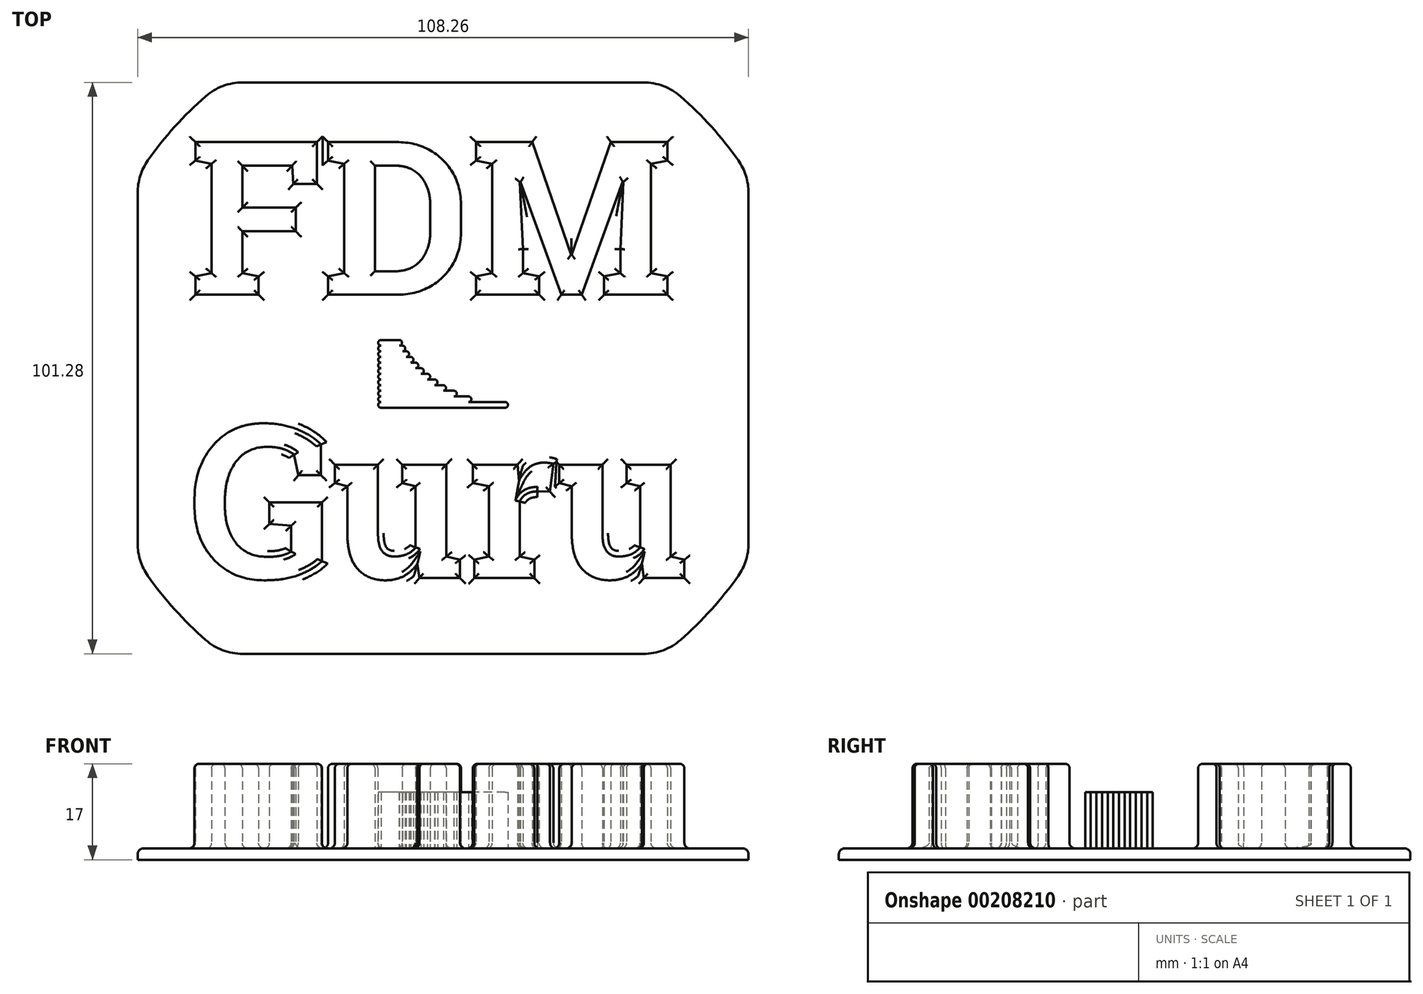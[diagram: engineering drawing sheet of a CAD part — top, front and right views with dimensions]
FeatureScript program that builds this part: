
annotation { "Feature Type Name" : "Feature", "Feature Type Description" : "" }
export const myFeature = defineFeature(function(context is Context, id is Id, definition is map)
    precondition{}
    {
        {
            var Q0;
            Q0=qCreatedBy(makeId("Top.planeOp"),FACE);
            var sketch = newSketch(context, id + "F0", { "sketchPlane" : qUnion([Q0])});
            skText(sketch, "E0", { "text": "FDM\nGuru", "fontName": "RobotoSlab-Bold.ttf"});
            const initialGuessF0  = {"E0": [-0.04493, 0.0016, 1, 0, 0.0274]};
            skSetInitialGuess(sketch, initialGuessF0);
            skSolve(sketch);
        }
        {
            var Q0;
            Q0 = qSketchRegion(id + "F0", true);
            extrude(context, id + "F1", {"entities" : qUnion([Q0]), "depth" : 15 * mm});
        }
        {
            var Q0;
            Q0=qCreatedBy(makeId("Top.planeOp"),FACE);
            var sketch = newSketch(context, id + "F2", { "sketchPlane" : qUnion([Q0])});
            skCircle(sketch, "E1", {"center": v(0, -11.42) * mm, "radius": 63.97 * mm});
            skLineSegment(sketch, "E2.bottom", {"start": v(54.13, -62.06) * mm, "end": v(-54.13, -62.06) * mm});
            skLineSegment(sketch, "E2.top", {"start": v(54.13, 39.22) * mm, "end": v(-54.13, 39.22) * mm});
            skLineSegment(sketch, "E2.left", {"start": v(54.13, -62.06) * mm, "end": v(54.13, 39.22) * mm});
            skLineSegment(sketch, "E2.right", {"start": v(-54.13, -62.06) * mm, "end": v(-54.13, 39.22) * mm});
            skSolve(sketch);
        }
        {
            var Q0;
            {var subQ1=sQuery(id+"F2.wireOp",EDGE,"E1");var subQ9=sQuery(id+"F2.wireOp",EDGE,"E2.top");var subQ11=makeQuery(id+"F2.imprint","INTERSECT",VERTEX,{"disambiguationData":[OD(0.0)],"derivedFrom":[subQ1,subQ9]});Q0=makeQuery(id+"F2.imprint","IMPRINT",FACE,{"disambiguationData":[TD([[makeQuery(id+"F2.imprint","IMPRINT",EDGE,{"disambiguationData":[TD([[subQ11,1.0]])],"derivedFrom":subQ1}),1.0]])]});}
            extrude(context, id + "F3", {"entities" : qUnion([Q0]), "operationType" : NewBodyOperationType.ADD, "oppositeDirection" : true, "depth" : 2 * mm});
        }
        {
            var Q0;
            Q0=makeQuery(id+"F1.opExtrude","CAP_FACE",FACE,{"disambiguationData":[OSD([sQuery(id+"F0.wireOp",EDGE,"E0.sketch_text.stroke-0"),sQuery(id+"F0.wireOp",EDGE,"E0.sketch_text.stroke-1"),sQuery(id+"F0.wireOp",EDGE,"E0.sketch_text.stroke-2"),sQuery(id+"F0.wireOp",EDGE,"E0.sketch_text.stroke-3"),sQuery(id+"F0.wireOp",EDGE,"E0.sketch_text.stroke-4"),sQuery(id+"F0.wireOp",EDGE,"E0.sketch_text.stroke-5"),sQuery(id+"F0.wireOp",EDGE,"E0.sketch_text.stroke-6"),sQuery(id+"F0.wireOp",EDGE,"E0.sketch_text.stroke-7"),sQuery(id+"F0.wireOp",EDGE,"E0.sketch_text.stroke-8"),sQuery(id+"F0.wireOp",EDGE,"E0.sketch_text.stroke-9"),sQuery(id+"F0.wireOp",EDGE,"E0.sketch_text.stroke-10"),sQuery(id+"F0.wireOp",EDGE,"E0.sketch_text.stroke-11"),sQuery(id+"F0.wireOp",EDGE,"E0.sketch_text.stroke-12"),sQuery(id+"F0.wireOp",EDGE,"E0.sketch_text.stroke-13"),sQuery(id+"F0.wireOp",EDGE,"E0.sketch_text.stroke-14"),sQuery(id+"F0.wireOp",EDGE,"E0.sketch_text.stroke-15"),sQuery(id+"F0.wireOp",EDGE,"E0.sketch_text.stroke-16"),sQuery(id+"F0.wireOp",EDGE,"E0.sketch_text.stroke-17")])],"isStart":false});
            var Q1;
            Q1=makeQuery(id+"F1.opExtrude","CAP_FACE",FACE,{"disambiguationData":[OSD([sQuery(id+"F0.wireOp",EDGE,"E0.sketch_text.stroke-18"),sQuery(id+"F0.wireOp",EDGE,"E0.sketch_text.stroke-19"),sQuery(id+"F0.wireOp",EDGE,"E0.sketch_text.stroke-20"),sQuery(id+"F0.wireOp",EDGE,"E0.sketch_text.stroke-21"),sQuery(id+"F0.wireOp",EDGE,"E0.sketch_text.stroke-22"),sQuery(id+"F0.wireOp",EDGE,"E0.sketch_text.stroke-23"),sQuery(id+"F0.wireOp",EDGE,"E0.sketch_text.stroke-24"),sQuery(id+"F0.wireOp",EDGE,"E0.sketch_text.stroke-25"),sQuery(id+"F0.wireOp",EDGE,"E0.sketch_text.stroke-26"),sQuery(id+"F0.wireOp",EDGE,"E0.sketch_text.stroke-27"),sQuery(id+"F0.wireOp",EDGE,"E0.sketch_text.stroke-28"),sQuery(id+"F0.wireOp",EDGE,"E0.sketch_text.stroke-29"),sQuery(id+"F0.wireOp",EDGE,"E0.sketch_text.stroke-30"),sQuery(id+"F0.wireOp",EDGE,"E0.sketch_text.stroke-31"),sQuery(id+"F0.wireOp",EDGE,"E0.sketch_text.stroke-32"),sQuery(id+"F0.wireOp",EDGE,"E0.sketch_text.stroke-33"),sQuery(id+"F0.wireOp",EDGE,"E0.sketch_text.stroke-34"),sQuery(id+"F0.wireOp",EDGE,"E0.sketch_text.stroke-35"),sQuery(id+"F0.wireOp",EDGE,"E0.sketch_text.stroke-36"),sQuery(id+"F0.wireOp",EDGE,"E0.sketch_text.stroke-37"),sQuery(id+"F0.wireOp",EDGE,"E0.sketch_text.stroke-38")])],"isStart":false});
            var Q2;
            Q2=makeQuery(id+"F1.opExtrude","CAP_FACE",FACE,{"disambiguationData":[OSD([sQuery(id+"F0.wireOp",EDGE,"E0.sketch_text.stroke-39"),sQuery(id+"F0.wireOp",EDGE,"E0.sketch_text.stroke-40"),sQuery(id+"F0.wireOp",EDGE,"E0.sketch_text.stroke-41"),sQuery(id+"F0.wireOp",EDGE,"E0.sketch_text.stroke-42"),sQuery(id+"F0.wireOp",EDGE,"E0.sketch_text.stroke-43"),sQuery(id+"F0.wireOp",EDGE,"E0.sketch_text.stroke-44"),sQuery(id+"F0.wireOp",EDGE,"E0.sketch_text.stroke-45"),sQuery(id+"F0.wireOp",EDGE,"E0.sketch_text.stroke-46"),sQuery(id+"F0.wireOp",EDGE,"E0.sketch_text.stroke-47"),sQuery(id+"F0.wireOp",EDGE,"E0.sketch_text.stroke-48"),sQuery(id+"F0.wireOp",EDGE,"E0.sketch_text.stroke-49"),sQuery(id+"F0.wireOp",EDGE,"E0.sketch_text.stroke-50"),sQuery(id+"F0.wireOp",EDGE,"E0.sketch_text.stroke-51"),sQuery(id+"F0.wireOp",EDGE,"E0.sketch_text.stroke-52"),sQuery(id+"F0.wireOp",EDGE,"E0.sketch_text.stroke-53"),sQuery(id+"F0.wireOp",EDGE,"E0.sketch_text.stroke-54"),sQuery(id+"F0.wireOp",EDGE,"E0.sketch_text.stroke-55"),sQuery(id+"F0.wireOp",EDGE,"E0.sketch_text.stroke-56"),sQuery(id+"F0.wireOp",EDGE,"E0.sketch_text.stroke-57"),sQuery(id+"F0.wireOp",EDGE,"E0.sketch_text.stroke-58"),sQuery(id+"F0.wireOp",EDGE,"E0.sketch_text.stroke-59"),sQuery(id+"F0.wireOp",EDGE,"E0.sketch_text.stroke-60"),sQuery(id+"F0.wireOp",EDGE,"E0.sketch_text.stroke-61"),sQuery(id+"F0.wireOp",EDGE,"E0.sketch_text.stroke-62"),sQuery(id+"F0.wireOp",EDGE,"E0.sketch_text.stroke-63"),sQuery(id+"F0.wireOp",EDGE,"E0.sketch_text.stroke-64"),sQuery(id+"F0.wireOp",EDGE,"E0.sketch_text.stroke-65"),sQuery(id+"F0.wireOp",EDGE,"E0.sketch_text.stroke-66"),sQuery(id+"F0.wireOp",EDGE,"E0.sketch_text.stroke-67"),sQuery(id+"F0.wireOp",EDGE,"E0.sketch_text.stroke-68"),sQuery(id+"F0.wireOp",EDGE,"E0.sketch_text.stroke-69")])],"isStart":false});
            var Q3;
            Q3=makeQuery(id+"F1.opExtrude","CAP_FACE",FACE,{"disambiguationData":[OSD([sQuery(id+"F0.wireOp",EDGE,"E0.sketch_text.stroke-139"),sQuery(id+"F0.wireOp",EDGE,"E0.sketch_text.stroke-140"),sQuery(id+"F0.wireOp",EDGE,"E0.sketch_text.stroke-141"),sQuery(id+"F0.wireOp",EDGE,"E0.sketch_text.stroke-142"),sQuery(id+"F0.wireOp",EDGE,"E0.sketch_text.stroke-143"),sQuery(id+"F0.wireOp",EDGE,"E0.sketch_text.stroke-144"),sQuery(id+"F0.wireOp",EDGE,"E0.sketch_text.stroke-145"),sQuery(id+"F0.wireOp",EDGE,"E0.sketch_text.stroke-146"),sQuery(id+"F0.wireOp",EDGE,"E0.sketch_text.stroke-147"),sQuery(id+"F0.wireOp",EDGE,"E0.sketch_text.stroke-148"),sQuery(id+"F0.wireOp",EDGE,"E0.sketch_text.stroke-149"),sQuery(id+"F0.wireOp",EDGE,"E0.sketch_text.stroke-150"),sQuery(id+"F0.wireOp",EDGE,"E0.sketch_text.stroke-151"),sQuery(id+"F0.wireOp",EDGE,"E0.sketch_text.stroke-152"),sQuery(id+"F0.wireOp",EDGE,"E0.sketch_text.stroke-153"),sQuery(id+"F0.wireOp",EDGE,"E0.sketch_text.stroke-154"),sQuery(id+"F0.wireOp",EDGE,"E0.sketch_text.stroke-155"),sQuery(id+"F0.wireOp",EDGE,"E0.sketch_text.stroke-156"),sQuery(id+"F0.wireOp",EDGE,"E0.sketch_text.stroke-157"),sQuery(id+"F0.wireOp",EDGE,"E0.sketch_text.stroke-158"),sQuery(id+"F0.wireOp",EDGE,"E0.sketch_text.stroke-159"),sQuery(id+"F0.wireOp",EDGE,"E0.sketch_text.stroke-160"),sQuery(id+"F0.wireOp",EDGE,"E0.sketch_text.stroke-161"),sQuery(id+"F0.wireOp",EDGE,"E0.sketch_text.stroke-162")])],"isStart":false});
            var Q4;
            Q4=makeQuery(id+"F1.opExtrude","CAP_FACE",FACE,{"disambiguationData":[OSD([sQuery(id+"F0.wireOp",EDGE,"E0.sketch_text.stroke-120"),sQuery(id+"F0.wireOp",EDGE,"E0.sketch_text.stroke-121"),sQuery(id+"F0.wireOp",EDGE,"E0.sketch_text.stroke-122"),sQuery(id+"F0.wireOp",EDGE,"E0.sketch_text.stroke-123"),sQuery(id+"F0.wireOp",EDGE,"E0.sketch_text.stroke-124"),sQuery(id+"F0.wireOp",EDGE,"E0.sketch_text.stroke-125"),sQuery(id+"F0.wireOp",EDGE,"E0.sketch_text.stroke-126"),sQuery(id+"F0.wireOp",EDGE,"E0.sketch_text.stroke-127"),sQuery(id+"F0.wireOp",EDGE,"E0.sketch_text.stroke-128"),sQuery(id+"F0.wireOp",EDGE,"E0.sketch_text.stroke-129"),sQuery(id+"F0.wireOp",EDGE,"E0.sketch_text.stroke-130"),sQuery(id+"F0.wireOp",EDGE,"E0.sketch_text.stroke-131"),sQuery(id+"F0.wireOp",EDGE,"E0.sketch_text.stroke-132"),sQuery(id+"F0.wireOp",EDGE,"E0.sketch_text.stroke-133"),sQuery(id+"F0.wireOp",EDGE,"E0.sketch_text.stroke-134"),sQuery(id+"F0.wireOp",EDGE,"E0.sketch_text.stroke-135"),sQuery(id+"F0.wireOp",EDGE,"E0.sketch_text.stroke-136"),sQuery(id+"F0.wireOp",EDGE,"E0.sketch_text.stroke-137"),sQuery(id+"F0.wireOp",EDGE,"E0.sketch_text.stroke-138")])],"isStart":false});
            var Q5;
            Q5=makeQuery(id+"F1.opExtrude","CAP_FACE",FACE,{"disambiguationData":[OSD([sQuery(id+"F0.wireOp",EDGE,"E0.sketch_text.stroke-96"),sQuery(id+"F0.wireOp",EDGE,"E0.sketch_text.stroke-97"),sQuery(id+"F0.wireOp",EDGE,"E0.sketch_text.stroke-98"),sQuery(id+"F0.wireOp",EDGE,"E0.sketch_text.stroke-99"),sQuery(id+"F0.wireOp",EDGE,"E0.sketch_text.stroke-100"),sQuery(id+"F0.wireOp",EDGE,"E0.sketch_text.stroke-101"),sQuery(id+"F0.wireOp",EDGE,"E0.sketch_text.stroke-102"),sQuery(id+"F0.wireOp",EDGE,"E0.sketch_text.stroke-103"),sQuery(id+"F0.wireOp",EDGE,"E0.sketch_text.stroke-104"),sQuery(id+"F0.wireOp",EDGE,"E0.sketch_text.stroke-105"),sQuery(id+"F0.wireOp",EDGE,"E0.sketch_text.stroke-106"),sQuery(id+"F0.wireOp",EDGE,"E0.sketch_text.stroke-107"),sQuery(id+"F0.wireOp",EDGE,"E0.sketch_text.stroke-108"),sQuery(id+"F0.wireOp",EDGE,"E0.sketch_text.stroke-109"),sQuery(id+"F0.wireOp",EDGE,"E0.sketch_text.stroke-110"),sQuery(id+"F0.wireOp",EDGE,"E0.sketch_text.stroke-111"),sQuery(id+"F0.wireOp",EDGE,"E0.sketch_text.stroke-112"),sQuery(id+"F0.wireOp",EDGE,"E0.sketch_text.stroke-113"),sQuery(id+"F0.wireOp",EDGE,"E0.sketch_text.stroke-114"),sQuery(id+"F0.wireOp",EDGE,"E0.sketch_text.stroke-115"),sQuery(id+"F0.wireOp",EDGE,"E0.sketch_text.stroke-116"),sQuery(id+"F0.wireOp",EDGE,"E0.sketch_text.stroke-117"),sQuery(id+"F0.wireOp",EDGE,"E0.sketch_text.stroke-118"),sQuery(id+"F0.wireOp",EDGE,"E0.sketch_text.stroke-119")])],"isStart":false});
            var Q6;
            Q6=makeQuery(id+"F1.opExtrude","CAP_FACE",FACE,{"disambiguationData":[OSD([sQuery(id+"F0.wireOp",EDGE,"E0.sketch_text.stroke-70"),sQuery(id+"F0.wireOp",EDGE,"E0.sketch_text.stroke-71"),sQuery(id+"F0.wireOp",EDGE,"E0.sketch_text.stroke-72"),sQuery(id+"F0.wireOp",EDGE,"E0.sketch_text.stroke-73"),sQuery(id+"F0.wireOp",EDGE,"E0.sketch_text.stroke-74"),sQuery(id+"F0.wireOp",EDGE,"E0.sketch_text.stroke-75"),sQuery(id+"F0.wireOp",EDGE,"E0.sketch_text.stroke-76"),sQuery(id+"F0.wireOp",EDGE,"E0.sketch_text.stroke-77"),sQuery(id+"F0.wireOp",EDGE,"E0.sketch_text.stroke-78"),sQuery(id+"F0.wireOp",EDGE,"E0.sketch_text.stroke-79"),sQuery(id+"F0.wireOp",EDGE,"E0.sketch_text.stroke-80"),sQuery(id+"F0.wireOp",EDGE,"E0.sketch_text.stroke-81"),sQuery(id+"F0.wireOp",EDGE,"E0.sketch_text.stroke-82"),sQuery(id+"F0.wireOp",EDGE,"E0.sketch_text.stroke-83"),sQuery(id+"F0.wireOp",EDGE,"E0.sketch_text.stroke-84"),sQuery(id+"F0.wireOp",EDGE,"E0.sketch_text.stroke-85"),sQuery(id+"F0.wireOp",EDGE,"E0.sketch_text.stroke-86"),sQuery(id+"F0.wireOp",EDGE,"E0.sketch_text.stroke-87"),sQuery(id+"F0.wireOp",EDGE,"E0.sketch_text.stroke-88"),sQuery(id+"F0.wireOp",EDGE,"E0.sketch_text.stroke-89"),sQuery(id+"F0.wireOp",EDGE,"E0.sketch_text.stroke-90"),sQuery(id+"F0.wireOp",EDGE,"E0.sketch_text.stroke-91"),sQuery(id+"F0.wireOp",EDGE,"E0.sketch_text.stroke-92"),sQuery(id+"F0.wireOp",EDGE,"E0.sketch_text.stroke-93"),sQuery(id+"F0.wireOp",EDGE,"E0.sketch_text.stroke-94"),sQuery(id+"F0.wireOp",EDGE,"E0.sketch_text.stroke-95")])],"isStart":false});
            fillet(context, id + "F4", {"entities" : qUnion([Q0, Q1, Q2, Q3, Q4, Q5, Q6]), "radius" : .8 * mm, "tangentPropagation" : true, "allowEdgeOverflow" : false});
        }
        {
            var Q0;
            {var subQ0=sQuery(id+"F2.wireOp",EDGE,"E1");Q0=makeQuery(id+"F3.boolean.opBoolean","SPLIT",FACE,{"disambiguationData":[TD([makeQuery(id+"F1.opExtrude","SWEPT_FACE",FACE,{"disambiguationData":[OSD([sQuery(id+"F0.wireOp",EDGE,"E0.sketch_text.stroke-0")])]})])],"derivedFrom":makeQuery(id+"F3.opExtrude","CAP_FACE",FACE,{"disambiguationData":[OSD([subQ0])],"isStart":true})});}
            fillet(context, id + "F5", {"entities" : qUnion([Q0]), "radius" : 1 * mm, "tangentPropagation" : true, "allowEdgeOverflow" : false});
        }
        {
            var Q0;
            {var subQ0=sQuery(id+"F2.wireOp",EDGE,"E1");Q0=makeQuery(id+"F3.boolean.opBoolean","SPLIT",FACE,{"disambiguationData":[TD([makeQuery(id+"F1.opExtrude","SWEPT_FACE",FACE,{"disambiguationData":[OSD([sQuery(id+"F0.wireOp",EDGE,"E0.sketch_text.stroke-0")])]})])],"derivedFrom":makeQuery(id+"F3.opExtrude","CAP_FACE",FACE,{"disambiguationData":[OSD([subQ0])],"isStart":true})});}
            var sketch = newSketch(context, id + "F6", { "sketchPlane" : qUnion([Q0])});
            skLineSegment(sketch, "E3.bottom", {"start": v(11, -18.43) * mm, "end": v(-11, -18.43) * mm});
            skLineSegment(sketch, "E3.top", {"start": v(11, -17.43) * mm, "end": v(-11, -17.43) * mm});
            skLineSegment(sketch, "E3.left", {"start": v(11, -18.43) * mm, "end": v(11, -17.43) * mm});
            skLineSegment(sketch, "E3.right", {"start": v(-11, -18.43) * mm, "end": v(-11, -17.43) * mm});
            skPoint(sketch, "E3.middle", {"position": v(0, -17.93) * mm});
            skArc(sketch, "E4", {"start": v(-11, -17.43) * mm, "mid": v(-11.5, -17.93) * mm, "end": v(-11, -18.43) * mm});
            skArc(sketch, "E5", {"start": v(11, -18.43) * mm, "mid": v(11.5, -17.93) * mm, "end": v(11, -17.43) * mm});
            skLineSegment(sketch, "E6.1.0.0", {"start": v(11, -16.43) * mm, "end": v(-11, -16.43) * mm});
            skArc(sketch, "E6.1.0.2", {"start": v(-11, -16.43) * mm, "mid": v(-11.5, -16.93) * mm, "end": v(-11, -17.43) * mm});
            skLineSegment(sketch, "E6.2.0.0", {"start": v(11, -15.43) * mm, "end": v(-11, -15.43) * mm});
            skLineSegment(sketch, "E6.2.0.1", {"start": v(11, -16.43) * mm, "end": v(-11, -16.43) * mm});
            skArc(sketch, "E6.2.0.2", {"start": v(-11, -15.43) * mm, "mid": v(-11.5, -15.93) * mm, "end": v(-11, -16.43) * mm});
            skLineSegment(sketch, "E6.3.0.0", {"start": v(11, -14.43) * mm, "end": v(-11, -14.43) * mm});
            skLineSegment(sketch, "E6.3.0.1", {"start": v(11, -15.43) * mm, "end": v(-11, -15.43) * mm});
            skArc(sketch, "E6.3.0.2", {"start": v(-11, -14.43) * mm, "mid": v(-11.5, -14.93) * mm, "end": v(-11, -15.43) * mm});
            skLineSegment(sketch, "E6.4.0.0", {"start": v(11, -13.43) * mm, "end": v(-11, -13.43) * mm});
            skLineSegment(sketch, "E6.4.0.1", {"start": v(11, -14.43) * mm, "end": v(-11, -14.43) * mm});
            skArc(sketch, "E6.4.0.2", {"start": v(-11, -13.43) * mm, "mid": v(-11.5, -13.93) * mm, "end": v(-11, -14.43) * mm});
            skLineSegment(sketch, "E6.5.0.0", {"start": v(11, -12.43) * mm, "end": v(-11, -12.43) * mm});
            skLineSegment(sketch, "E6.5.0.1", {"start": v(11, -13.43) * mm, "end": v(-11, -13.43) * mm});
            skArc(sketch, "E6.5.0.2", {"start": v(-11, -12.43) * mm, "mid": v(-11.5, -12.93) * mm, "end": v(-11, -13.43) * mm});
            skLineSegment(sketch, "E6.direction1", {"start": v(-11, -17.43) * mm, "end": v(-11, -16.43) * mm, "construction": true});
            skLineSegment(sketch, "E7.0.6.0", {"start": v(11, -11.43) * mm, "end": v(-11, -11.43) * mm});
            skArc(sketch, "E7.6.6.0", {"start": v(-11, -11.43) * mm, "mid": v(-11.5, -11.93) * mm, "end": v(-11, -12.43) * mm});
            skLineSegment(sketch, "E7.0.7.0", {"start": v(11, -10.43) * mm, "end": v(-11, -10.43) * mm});
            skLineSegment(sketch, "E7.3.7.0", {"start": v(11, -11.43) * mm, "end": v(-11, -11.43) * mm});
            skArc(sketch, "E7.6.7.0", {"start": v(-11, -10.43) * mm, "mid": v(-11.5, -10.93) * mm, "end": v(-11, -11.43) * mm});
            skLineSegment(sketch, "E7.0.8.0", {"start": v(11, -9.43) * mm, "end": v(-11, -9.43) * mm});
            skLineSegment(sketch, "E7.3.8.0", {"start": v(11, -10.43) * mm, "end": v(-11, -10.43) * mm});
            skArc(sketch, "E7.6.8.0", {"start": v(-11, -9.43) * mm, "mid": v(-11.5, -9.93) * mm, "end": v(-11, -10.43) * mm});
            skLineSegment(sketch, "E7.0.9.0", {"start": v(11, -8.43) * mm, "end": v(-11, -8.43) * mm});
            skLineSegment(sketch, "E7.3.9.0", {"start": v(11, -9.43) * mm, "end": v(-11, -9.43) * mm});
            skArc(sketch, "E7.6.9.0", {"start": v(-11, -8.43) * mm, "mid": v(-11.5, -8.93) * mm, "end": v(-11, -9.43) * mm});
            skLineSegment(sketch, "E7.0.10.0", {"start": v(11, -7.43) * mm, "end": v(-11, -7.43) * mm});
            skLineSegment(sketch, "E7.3.10.0", {"start": v(11, -8.43) * mm, "end": v(-11, -8.43) * mm});
            skArc(sketch, "E7.6.10.0", {"start": v(-11, -7.43) * mm, "mid": v(-11.5, -7.93) * mm, "end": v(-11, -8.43) * mm});
            skLineSegment(sketch, "E7.0.11.0", {"start": v(11, -6.43) * mm, "end": v(-11, -6.43) * mm});
            skLineSegment(sketch, "E7.3.11.0", {"start": v(11, -7.43) * mm, "end": v(-11, -7.43) * mm});
            skArc(sketch, "E7.6.11.0", {"start": v(-11, -6.43) * mm, "mid": v(-11.5, -6.93) * mm, "end": v(-11, -7.43) * mm});
            skLineSegment(sketch, "E8", {"start": v(-7.79, -6.43) * mm, "end": v(-7.79, -7.43) * mm});
            skLineSegment(sketch, "E9", {"start": v(-7.2, -7.43) * mm, "end": v(-7.2, -8.43) * mm});
            skLineSegment(sketch, "E10", {"start": v(-6.52, -8.43) * mm, "end": v(-6.52, -9.43) * mm});
            skLineSegment(sketch, "E11", {"start": v(-5.75, -9.43) * mm, "end": v(-5.75, -10.43) * mm});
            skLineSegment(sketch, "E12", {"start": v(-4.9, -10.43) * mm, "end": v(-4.9, -11.43) * mm});
            skLineSegment(sketch, "E13", {"start": v(-3.92, -11.43) * mm, "end": v(-3.92, -12.43) * mm});
            skLineSegment(sketch, "E14", {"start": v(-2.8, -12.43) * mm, "end": v(-2.8, -13.43) * mm});
            skLineSegment(sketch, "E15", {"start": v(-1.5, -13.43) * mm, "end": v(-1.5, -14.43) * mm});
            skLineSegment(sketch, "E16", {"start": v(0.03, -14.43) * mm, "end": v(0.03, -15.43) * mm});
            skLineSegment(sketch, "E17", {"start": v(1.93, -15.43) * mm, "end": v(1.93, -16.43) * mm});
            skLineSegment(sketch, "E18", {"start": v(4.51, -16.43) * mm, "end": v(4.51, -17.43) * mm});
            skArc(sketch, "E19", {"start": v(-7.79, -7.43) * mm, "mid": v(-7.27, -6.93) * mm, "end": v(-7.79, -6.43) * mm});
            skArc(sketch, "E20", {"start": v(-7.2, -8.43) * mm, "mid": v(-6.7, -7.93) * mm, "end": v(-7.2, -7.43) * mm});
            skArc(sketch, "E21", {"start": v(-6.52, -9.43) * mm, "mid": v(-6.02, -8.93) * mm, "end": v(-6.52, -8.43) * mm});
            skArc(sketch, "E22", {"start": v(-5.75, -10.43) * mm, "mid": v(-5.25, -9.93) * mm, "end": v(-5.75, -9.43) * mm});
            skArc(sketch, "E23", {"start": v(-4.9, -11.43) * mm, "mid": v(-4.4, -10.93) * mm, "end": v(-4.9, -10.43) * mm});
            skArc(sketch, "E24", {"start": v(-3.92, -12.43) * mm, "mid": v(-3.42, -11.93) * mm, "end": v(-3.92, -11.43) * mm});
            skArc(sketch, "E25", {"start": v(-2.8, -13.43) * mm, "mid": v(-2.29, -12.93) * mm, "end": v(-2.8, -12.43) * mm});
            skArc(sketch, "E26", {"start": v(-1.5, -14.43) * mm, "mid": v(-0.98, -13.93) * mm, "end": v(-1.5, -13.43) * mm});
            skArc(sketch, "E27", {"start": v(0.03, -15.43) * mm, "mid": v(0.5, -14.93) * mm, "end": v(0.03, -14.43) * mm});
            skArc(sketch, "E28", {"start": v(1.93, -16.43) * mm, "mid": v(2.43, -15.93) * mm, "end": v(1.93, -15.43) * mm});
            skArc(sketch, "E29", {"start": v(4.51, -17.43) * mm, "mid": v(5, -16.93) * mm, "end": v(4.51, -16.43) * mm});
            skSolve(sketch);
        }
        {
            var Q0;
            Q0 = qSketchRegion(id + "F6", true);
            extrude(context, id + "F7", {"entities" : qUnion([Q0]), "operationType" : NewBodyOperationType.ADD, "depth" : 10 * mm});
        }
        {
            var Q0;
            Q0 = qSketchRegion(id + "F6", true);
            extrude(context, id + "F8", {"entities" : qUnion([Q0]), "operationType" : NewBodyOperationType.ADD, "depth" : 10 * mm});
        }
        {
            var Q0;
            {var subQ0=sQuery(id+"F2.wireOp",EDGE,"E2.top");var subQ1=sQuery(id+"F2.wireOp",EDGE,"E1");Q0=makeQuery(id+"F3.opExtrude","SWEPT_EDGE",EDGE,{"disambiguationData":[OSD([subQ1,subQ0]),TDD([makeQuery(id+"F2.imprint","INTERSECT",VERTEX,{"disambiguationData":[OD(0.0)],"derivedFrom":[subQ1,subQ0]})])]});}
            var Q1;
            {var subQ0=sQuery(id+"F2.wireOp",EDGE,"E2.left");var subQ1=sQuery(id+"F2.wireOp",EDGE,"E1");Q1=makeQuery(id+"F3.opExtrude","SWEPT_EDGE",EDGE,{"disambiguationData":[OSD([subQ1,subQ0]),TDD([makeQuery(id+"F2.imprint","INTERSECT",VERTEX,{"disambiguationData":[OD(0.0)],"derivedFrom":[subQ1,subQ0]})])]});}
            var Q2;
            {var subQ0=sQuery(id+"F2.wireOp",EDGE,"E2.left");var subQ1=sQuery(id+"F2.wireOp",EDGE,"E1");Q2=makeQuery(id+"F3.opExtrude","SWEPT_EDGE",EDGE,{"disambiguationData":[OSD([subQ1,subQ0]),TDD([makeQuery(id+"F2.imprint","INTERSECT",VERTEX,{"disambiguationData":[OD(1.0)],"derivedFrom":[subQ1,subQ0]})])]});}
            var Q3;
            {var subQ0=sQuery(id+"F2.wireOp",EDGE,"E2.bottom");var subQ1=sQuery(id+"F2.wireOp",EDGE,"E1");Q3=makeQuery(id+"F3.opExtrude","SWEPT_EDGE",EDGE,{"disambiguationData":[OSD([subQ1,subQ0]),TDD([makeQuery(id+"F2.imprint","INTERSECT",VERTEX,{"disambiguationData":[OD(1.0)],"derivedFrom":[subQ1,subQ0]})])]});}
            var Q4;
            {var subQ0=sQuery(id+"F2.wireOp",EDGE,"E2.bottom");var subQ1=sQuery(id+"F2.wireOp",EDGE,"E1");Q4=makeQuery(id+"F3.opExtrude","SWEPT_EDGE",EDGE,{"disambiguationData":[OSD([subQ1,subQ0]),TDD([makeQuery(id+"F2.imprint","INTERSECT",VERTEX,{"disambiguationData":[OD(0.0)],"derivedFrom":[subQ1,subQ0]})])]});}
            var Q5;
            {var subQ0=sQuery(id+"F2.wireOp",EDGE,"E2.right");var subQ1=sQuery(id+"F2.wireOp",EDGE,"E1");Q5=makeQuery(id+"F3.opExtrude","SWEPT_EDGE",EDGE,{"disambiguationData":[OSD([subQ1,subQ0]),TDD([makeQuery(id+"F2.imprint","INTERSECT",VERTEX,{"disambiguationData":[OD(1.0)],"derivedFrom":[subQ1,subQ0]})])]});}
            var Q6;
            {var subQ0=sQuery(id+"F2.wireOp",EDGE,"E2.right");var subQ1=sQuery(id+"F2.wireOp",EDGE,"E1");Q6=makeQuery(id+"F3.opExtrude","SWEPT_EDGE",EDGE,{"disambiguationData":[OSD([subQ1,subQ0]),TDD([makeQuery(id+"F2.imprint","INTERSECT",VERTEX,{"disambiguationData":[OD(0.0)],"derivedFrom":[subQ1,subQ0]})])]});}
            var Q7;
            {var subQ0=sQuery(id+"F2.wireOp",EDGE,"E2.top");var subQ1=sQuery(id+"F2.wireOp",EDGE,"E1");Q7=makeQuery(id+"F3.opExtrude","SWEPT_EDGE",EDGE,{"disambiguationData":[OSD([subQ1,subQ0]),TDD([makeQuery(id+"F2.imprint","INTERSECT",VERTEX,{"disambiguationData":[OD(1.0)],"derivedFrom":[subQ1,subQ0]})])]});}
            fillet(context, id + "F9", {"entities" : qUnion([Q0, Q1, Q2, Q3, Q4, Q5, Q6, Q7]), "radius" : 10 * mm, "tangentPropagation" : true, "allowEdgeOverflow" : false});
        }
    });
